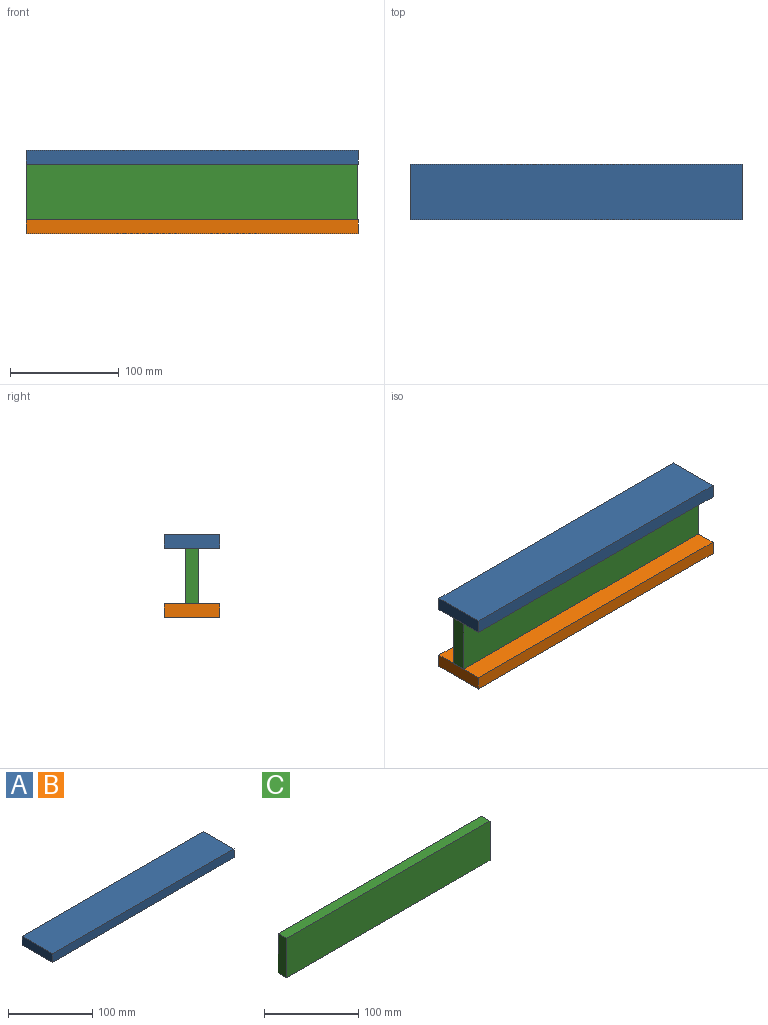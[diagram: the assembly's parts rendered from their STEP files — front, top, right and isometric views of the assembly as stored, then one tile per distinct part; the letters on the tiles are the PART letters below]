
ASSEMBLY  parts=3 mates=2
PART A: 6 faces, bbox 304.8x51x12.7 mm
  f0: plane 304.81x12.7mm, normal (0,1,0), area 3871.1mm2, adj f1,f3,f4,f5
  f1: plane 51x12.7mm, normal (-1,0,0), area 647.7mm2, adj f0,f2,f4,f5
  f2: plane 304.81x12.7mm, normal (0,-1,0), area 3871.1mm2, adj f1,f3,f4,f5
  f3: plane 51x12.7mm, normal (1,0,0), area 647.7mm2, adj f0,f2,f4,f5
  f4: plane 304.81x51mm, normal (0,0,1), area 15546.4mm2, adj f0,f1,f2,f3
  f5: plane 304.81x51mm, normal (0,0,-1), area 15546.4mm2, adj f0,f1,f2,f3
PART B: same geometry as A
PART C: 6 faces, bbox 304.8x12.8x51 mm
  f0: plane 304.8x12.81mm, normal (0,0,1), area 3904.9mm2, adj f1,f3,f4,f5
  f1: plane 304.8x51mm, normal (0,-1,0), area 15545.8mm2, adj f0,f2,f4,f5
  f2: plane 304.8x12.81mm, normal (0,0,-1), area 3904.9mm2, adj f1,f3,f4,f5
  f3: plane 304.8x51mm, normal (0,1,0), area 15545.8mm2, adj f0,f2,f4,f5
  f4: plane 51x12.81mm, normal (1,0,0), area 653.4mm2, adj f0,f1,f2,f3
  f5: plane 51x12.81mm, normal (-1,0,0), area 653.4mm2, adj f0,f1,f2,f3
PLACE A t=(34.83,-122.56,285.04)mm
PLACE B t=(34.83,-122.56,221.34)mm
PLACE C t=(-107.78,-121.95,292.42)mm
MATE fastened C.f0 <-> A.f5  axis (0,0,1) through (44.62,-86.78,285.04)mm
MATE fastened B.f4 <-> C.f2  axis (0,0,1) through (44.62,-86.78,234.04)mm
